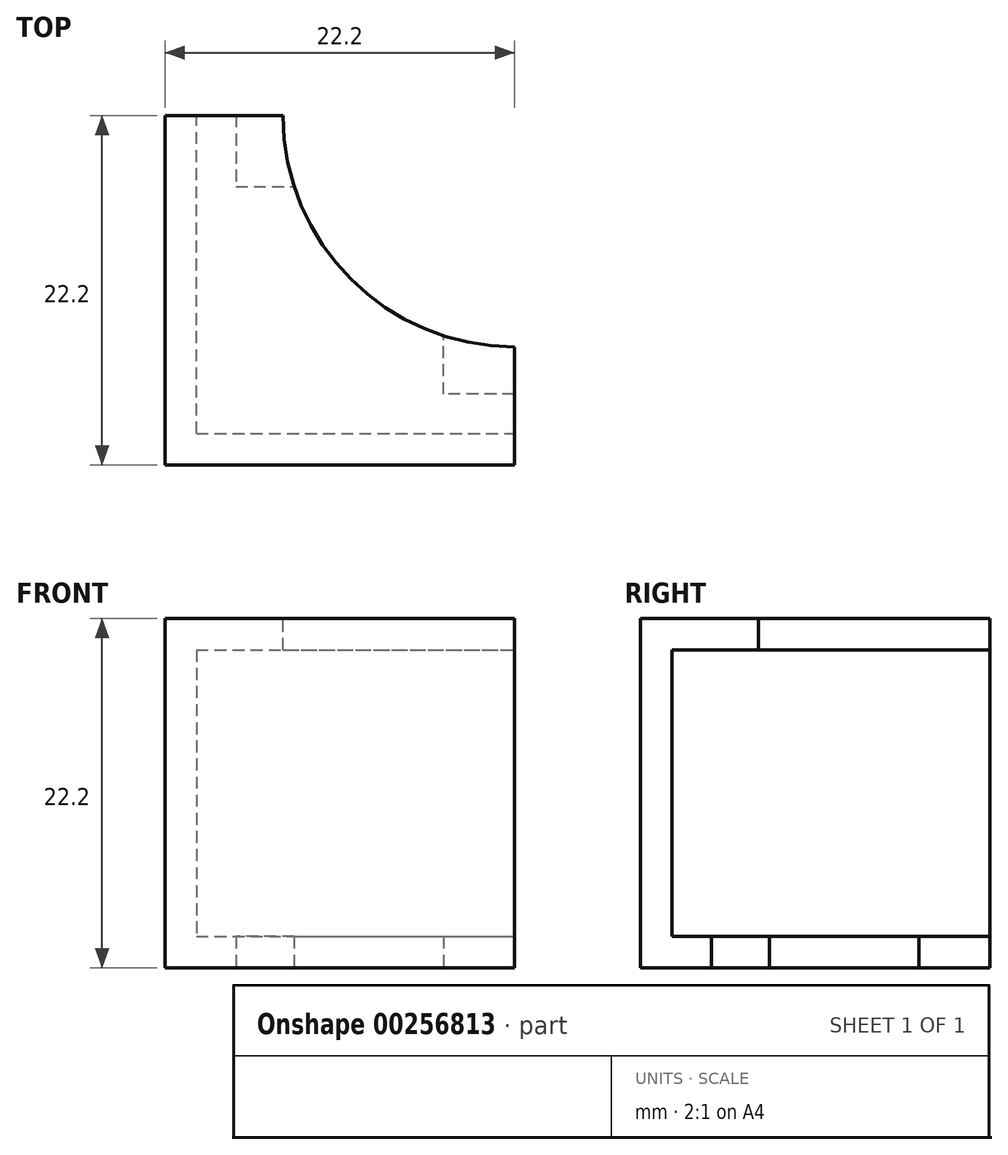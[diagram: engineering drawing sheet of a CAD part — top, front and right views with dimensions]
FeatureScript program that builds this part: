
annotation { "Feature Type Name" : "Feature", "Feature Type Description" : "" }
export const myFeature = defineFeature(function(context is Context, id is Id, definition is map)
    precondition{}
    {
        {
            var Q0;
            Q0=qCreatedBy(makeId("Front.planeOp"),FACE);
            var sketch = newSketch(context, id + "F0", { "sketchPlane" : qUnion([Q0])});
            skLineSegment(sketch, "E0.bottom", {"start": v(-22.2, 22.2) * mm, "end": v(0, 22.2) * mm});
            skLineSegment(sketch, "E0.top", {"start": v(-22.2, 0) * mm, "end": v(0, 0) * mm});
            skLineSegment(sketch, "E0.left", {"start": v(-22.2, 22.2) * mm, "end": v(-22.2, 0) * mm});
            skLineSegment(sketch, "E0.right", {"start": v(0, 22.2) * mm, "end": v(0, 0) * mm});
            skSolve(sketch);
        }
        {
            var Q0;
            Q0=makeQuery(id+"F0.imprint","IMPRINT",FACE,{"disambiguationData":[TD([[makeQuery(id+"F0.imprint","IMPRINT",EDGE,{"derivedFrom":sQuery(id+"F0.wireOp",EDGE,"E0.bottom")}),-1.0]])]});
            extrude(context, id + "F1", {"entities" : qUnion([Q0]), "depth" : 22.2 * mm});
        }
        {
            var Q0;
            Q0=makeQuery(id+"F1.opExtrude","SWEPT_FACE",FACE,{"disambiguationData":[OSD([sQuery(id+"F0.wireOp",EDGE,"E0.right")])]});
            var Q1;
            Q1=makeQuery(id+"F1.opExtrude","CAP_FACE",FACE,{"disambiguationData":[OSD([sQuery(id+"F0.wireOp",EDGE,"E0.bottom"),sQuery(id+"F0.wireOp",EDGE,"E0.top"),sQuery(id+"F0.wireOp",EDGE,"E0.left"),sQuery(id+"F0.wireOp",EDGE,"E0.right")])],"isStart":true});
            shell(context, id + "F2", {"entities" : qUnion([Q0, Q1]), "thickness" : 2 * mm});
        }
        {
            var Q0;
            Q0=makeQuery(id+"F1.opExtrude","SWEPT_FACE",FACE,{"disambiguationData":[OSD([sQuery(id+"F0.wireOp",EDGE,"E0.bottom")])]});
            var sketch = newSketch(context, id + "F3", { "sketchPlane" : qUnion([Q0])});
            skLineSegment(sketch, "E1", {"start": v(-22.2, 0) * mm, "end": v(-14.7, 0) * mm});
            skLineSegment(sketch, "E2", {"start": v(0, -14.7) * mm, "end": v(0, -22.2) * mm});
            skArc(sketch, "E3", {"start": v(-14.7, 0) * mm, "mid": v(-10.4, -10.4) * mm, "end": v(0, -14.7) * mm});
            skSolve(sketch);
        }
        {
            var Q0;
            {var subQ0=sQuery(id+"F3.wireOp",EDGE,"E3");Q0=makeQuery(id+"F3.imprint","IMPRINT",FACE,{"disambiguationData":[TD([[makeQuery(id+"F3.imprint","IMPRINT",EDGE,{"derivedFrom":subQ0}),1.0]])]});}
            extrude(context, id + "F4", {"entities" : qUnion([Q0]), "operationType" : NewBodyOperationType.REMOVE, "endBound" : BoundingType.THROUGH_ALL, "oppositeDirection" : true, "depth" : 25 * mm});
        }
        {
            var Q0;
            Q0=makeQuery(id+"F1.opExtrude","SWEPT_FACE",FACE,{"disambiguationData":[OSD([sQuery(id+"F0.wireOp",EDGE,"E0.top")])]});
            var sketch = newSketch(context, id + "F5", { "sketchPlane" : qUnion([Q0])});
            skLineSegment(sketch, "E4", {"start": v(-22.2, 0) * mm, "end": v(-17.7, 0) * mm});
            skLineSegment(sketch, "E5", {"start": v(-17.7, 0) * mm, "end": v(-17.7, 4.5) * mm});
            skLineSegment(sketch, "E6", {"start": v(-17.7, 4.5) * mm, "end": v(-14, 4.5) * mm});
            skLineSegment(sketch, "E7", {"start": v(0, 17.7) * mm, "end": v(-4.5, 17.7) * mm});
            skLineSegment(sketch, "E8", {"start": v(-4.5, 17.7) * mm, "end": v(-4.5, 14) * mm});
            skLineSegment(sketch, "E9", {"start": v(0, 17.7) * mm, "end": v(0, 22.2) * mm});
            skSolve(sketch);
        }
        {
            var Q0;
            {var subQ0=sQuery(id+"F5.wireOp",EDGE,"E5");Q0=makeQuery(id+"F5.imprint","IMPRINT",FACE,{"disambiguationData":[TD([[makeQuery(id+"F5.imprint","IMPRINT",EDGE,{"derivedFrom":subQ0}),-1.0]])]});}
            var Q1;
            {var subQ0=sQuery(id+"F5.wireOp",EDGE,"E7");Q1=makeQuery(id+"F5.imprint","IMPRINT",FACE,{"disambiguationData":[TD([[makeQuery(id+"F5.imprint","IMPRINT",EDGE,{"derivedFrom":subQ0}),1.0]])]});}
            extrude(context, id + "F6", {"entities" : qUnion([Q0, Q1]), "operationType" : NewBodyOperationType.REMOVE, "oppositeDirection" : true, "depth" : 2.5 * mm});
        }
    });
